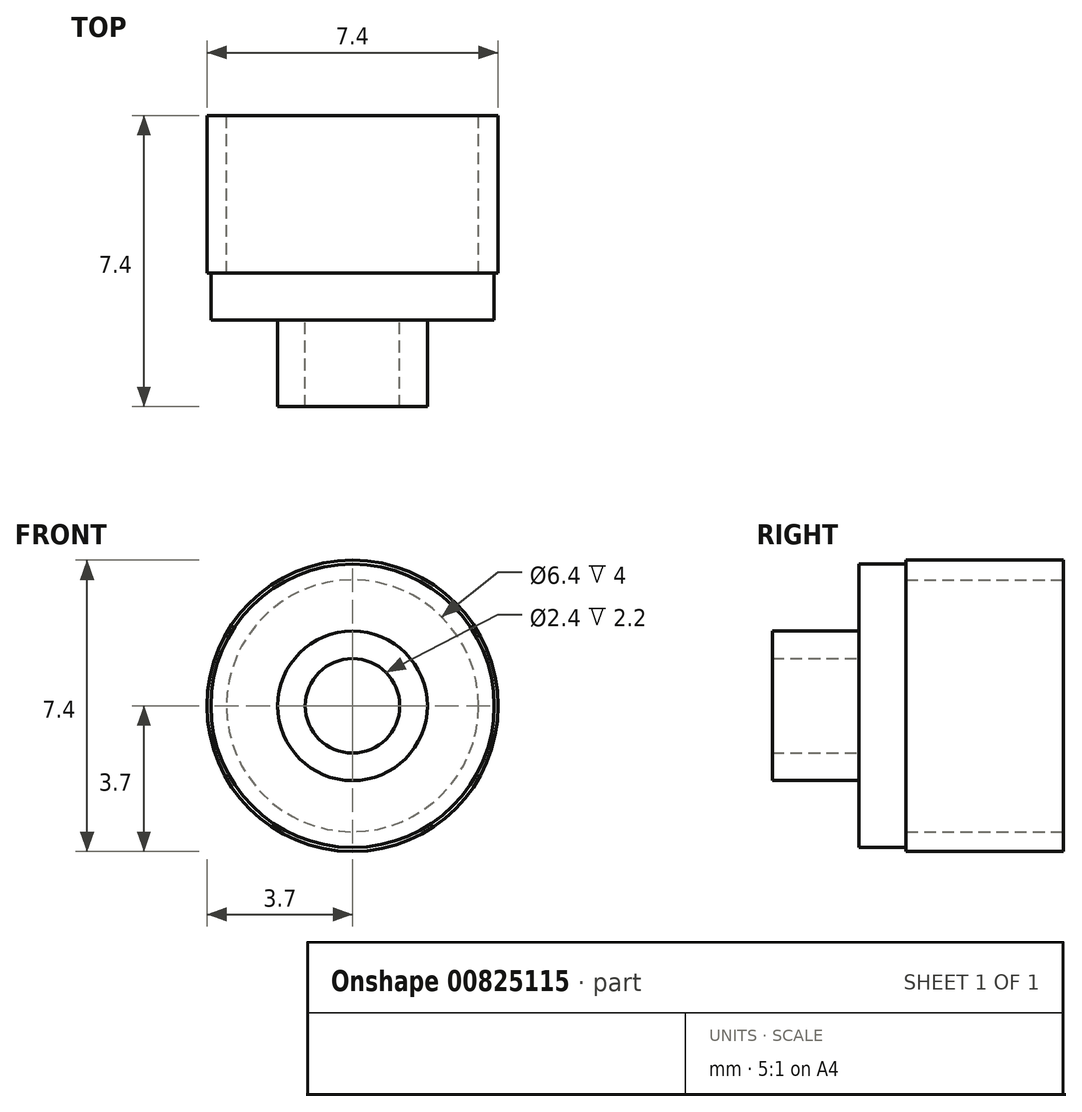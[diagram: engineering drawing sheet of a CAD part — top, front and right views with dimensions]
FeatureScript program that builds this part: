
annotation { "Feature Type Name" : "Feature", "Feature Type Description" : "" }
export const myFeature = defineFeature(function(context is Context, id is Id, definition is map)
    precondition{}
    {
        {
            var Q0;
            Q0=qCreatedBy(makeId("Front.planeOp"),FACE);
            var sketch = newSketch(context, id + "F0", { "sketchPlane" : qUnion([Q0])});
            skCircle(sketch, "E0", {"center": v(0, 0) * mm, "radius": 3.2 * mm});
            skCircle(sketch, "E1", {"center": v(0, 0) * mm, "radius": 3.7 * mm});
            skSolve(sketch);
        }
        {
            var Q0;
            Q0=makeQuery(id+"F0.imprint","IMPRINT",FACE,{"disambiguationData":[TD([[makeQuery(id+"F0.imprint","IMPRINT",EDGE,{"derivedFrom":sQuery(id+"F0.wireOp",EDGE,"E0")}),-1.0]])]});
            extrude(context, id + "F1", {"entities" : qUnion([Q0]), "depth" : 4 * mm, "offsetDistance" : 25 * mm});
        }
        {
            var Q0;
            Q0=makeQuery(id+"F1.opExtrude","CAP_FACE",FACE,{"disambiguationData":[OSD([sQuery(id+"F0.wireOp",EDGE,"E0"),sQuery(id+"F0.wireOp",EDGE,"E1")])],"isStart":false});
            var sketch = newSketch(context, id + "F2", { "sketchPlane" : qUnion([Q0])});
            skCircle(sketch, "E2", {"center": v(0, 0) * mm, "radius": 3.6 * mm});
            skSolve(sketch);
        }
        {
            var Q0;
            Q0 = qSketchRegion(id + "F2", true);
            extrude(context, id + "F3", {"entities" : qUnion([Q0]), "operationType" : NewBodyOperationType.ADD, "depth" : 1.2 * mm, "offsetDistance" : 25 * mm});
        }
        {
            var Q0;
            Q0=makeQuery(id+"F3.opExtrude","CAP_FACE",FACE,{"disambiguationData":[OSD([sQuery(id+"F2.wireOp",EDGE,"E2")])],"isStart":false});
            var sketch = newSketch(context, id + "F4", { "sketchPlane" : qUnion([Q0])});
            skCircle(sketch, "E3", {"center": v(0, 0) * mm, "radius": 1.2 * mm});
            skCircle(sketch, "E4", {"center": v(0, 0) * mm, "radius": 1.9 * mm});
            skSolve(sketch);
        }
        {
            var Q0;
            Q0=makeQuery(id+"F4.imprint","IMPRINT",FACE,{"disambiguationData":[TD([[makeQuery(id+"F4.imprint","IMPRINT",EDGE,{"derivedFrom":sQuery(id+"F4.wireOp",EDGE,"E3")}),-1.0]])]});
            extrude(context, id + "F5", {"entities" : qUnion([Q0]), "operationType" : NewBodyOperationType.ADD, "depth" : 2.2 * mm, "offsetDistance" : 25 * mm});
        }
    });
